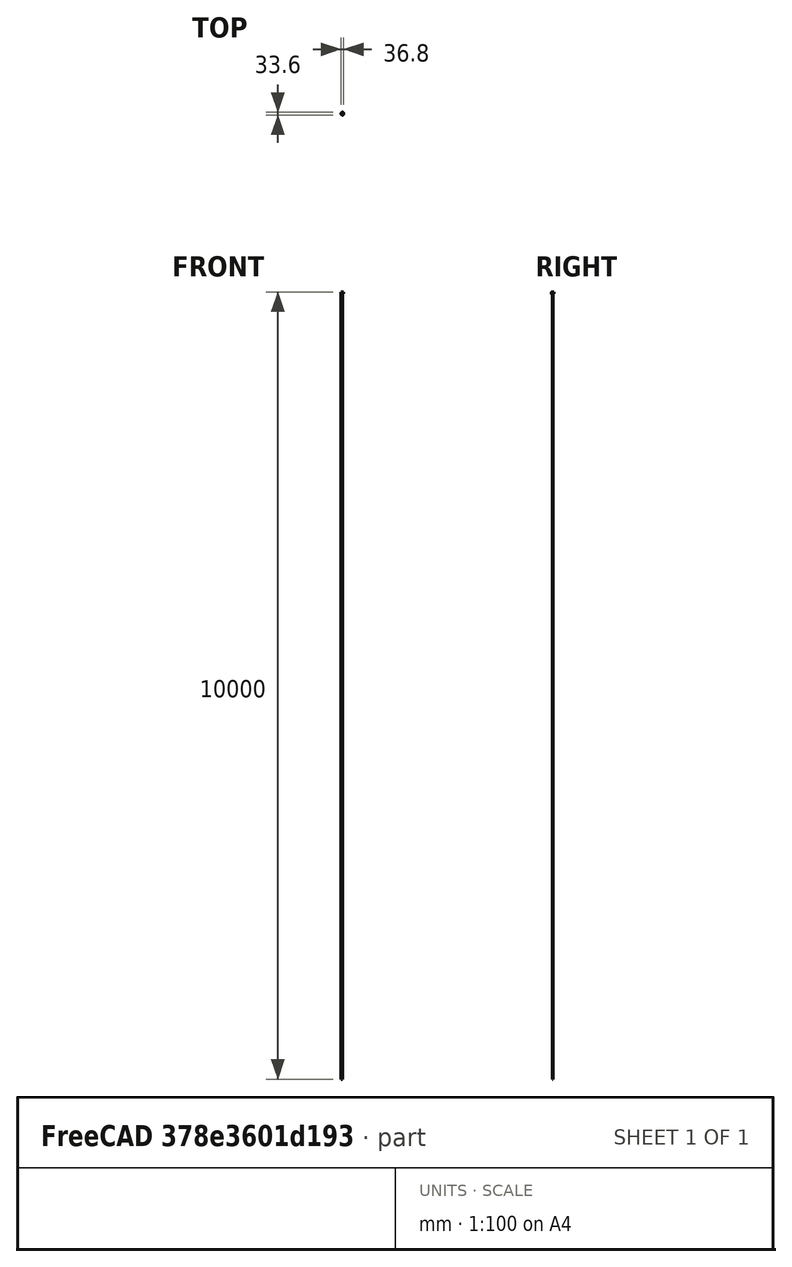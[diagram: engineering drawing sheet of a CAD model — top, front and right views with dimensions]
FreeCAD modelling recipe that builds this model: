
FCSTD DOCUMENT  (FreeCAD 0.16R)
Label: Spacer31.7-25.4
License: All rights reserved
LicenseURL: http://en.wikipedia.org/wiki/All_rights_reserved
objects: Sketcher::SketchObject×5, PartDesign::Pad×3, PartDesign::Pocket×2, PartDesign::Chamfer×2, Mesh::Feature×1
note: 17 computed .brp shape members not serialized (recipe doc carries the construction recipe); baked Part::Feature solids carry a one-line shape summary decoded from their .brp

FEATURE [Sketcher::SketchObject] Sketch
  sketch-geometry (1):
    g0: Circle CenterX=0 CenterY=0 CenterZ=0 NormalX=0 NormalY=0 NormalZ=1 Radius=15.8
  constraints (2):
    c: Coincident(g0,g-1)
    c: Radius(g0) = 15.8
FEATURE [PartDesign::Pad] Pad
  Length = 18.8
  Length2 = 100
  Sketch = -> Sketch
  Type = 0
FEATURE [Sketcher::SketchObject] Sketch003
  Placement = pos=(0,0,18.8) rot=(0,0,1;0rad)
  Support = -> Pad [Face3]
  sketch-geometry (1):
    g0: Circle CenterX=0 CenterY=0 CenterZ=0 NormalX=0 NormalY=0 NormalZ=1 Radius=16.8
  constraints (2):
    c: Radius(g0) = 16.8
    c: Coincident(g0,g-1)
FEATURE [PartDesign::Pad] Pad001
  Length = 1
  Length2 = 100
  Sketch = -> Sketch003
  Type = 0
FEATURE [Sketcher::SketchObject] Sketch004
  Placement = pos=(0,0,0) rot=(1,0,0;3.14159rad)
  Support = -> Pad001 [Face1]
  sketch-geometry (1):
    g0: Circle CenterX=0 CenterY=0 CenterZ=0 NormalX=0 NormalY=0 NormalZ=1 Radius=16.8
  constraints (2):
    c: Coincident(g0,g-1)
    c: Radius(g0) = 16.8
FEATURE [PartDesign::Pad] Pad002
  Length = 1
  Length2 = 100
  Sketch = -> Sketch004
  Type = 0
FEATURE [Sketcher::SketchObject] Sketch002
  Placement = pos=(0,0,19.8) rot=(0,0,1;0rad)
  Support = -> Pad002 [Face4]
  sketch-geometry (4):
    g0: LineSegment StartX=-20 StartY=1 StartZ=0 EndX=0 EndY=1 EndZ=0
    g1: LineSegment StartX=0 StartY=1 StartZ=0 EndX=0 EndY=-1 EndZ=0
    g2: LineSegment StartX=0 StartY=-1 StartZ=0 EndX=-20 EndY=-1 EndZ=0
    g3: LineSegment StartX=-20 StartY=-1 StartZ=0 EndX=-20 EndY=1 EndZ=0
  constraints (12):
    c: Coincident(g0,g1)
    c: Coincident(g1,g2)
    c: Coincident(g2,g3)
    c: Coincident(g3,g0)
    c: Horizontal(g0)
    c: Horizontal(g2)
    c: Vertical(g1)
    c: Vertical(g3)
    c: Symmetric(g1,g0,g-1)
    c: Distance(g3) = 2
    c: Distance(g0) = 20
    c: PointOnObject(g1,g-2)
FEATURE [PartDesign::Pocket] Pocket
  Length = 5
  Sketch = -> Sketch002
  Type = 1
FEATURE [Sketcher::SketchObject] Sketch001
  Placement = pos=(0,0,19.8) rot=(0,0,1;0rad)
  Support = -> Pocket [Face8]
  sketch-geometry (1):
    g0: Circle CenterX=0 CenterY=0 CenterZ=0 NormalX=0 NormalY=0 NormalZ=1 Radius=12.4
  constraints (2):
    c: Radius(g0) = 12.4
    c: Coincident(g0,g-1)
FEATURE [PartDesign::Pocket] Pocket001
  Length = 5
  Sketch = -> Sketch001
  Type = 1
FEATURE [PartDesign::Chamfer] Chamfer
  Base = -> Pocket001 [Edge19,Edge11,Edge25,Edge23,Edge13,Edge9,Edge21,Edge15]
  Size = 0.5
FEATURE [PartDesign::Chamfer] Chamfer001
  Base = -> Chamfer [Edge1,Edge58]
  Size = 0.9
FEATURE [Mesh::Feature] Mesh  label="Chamfer001 (Meshed)"
